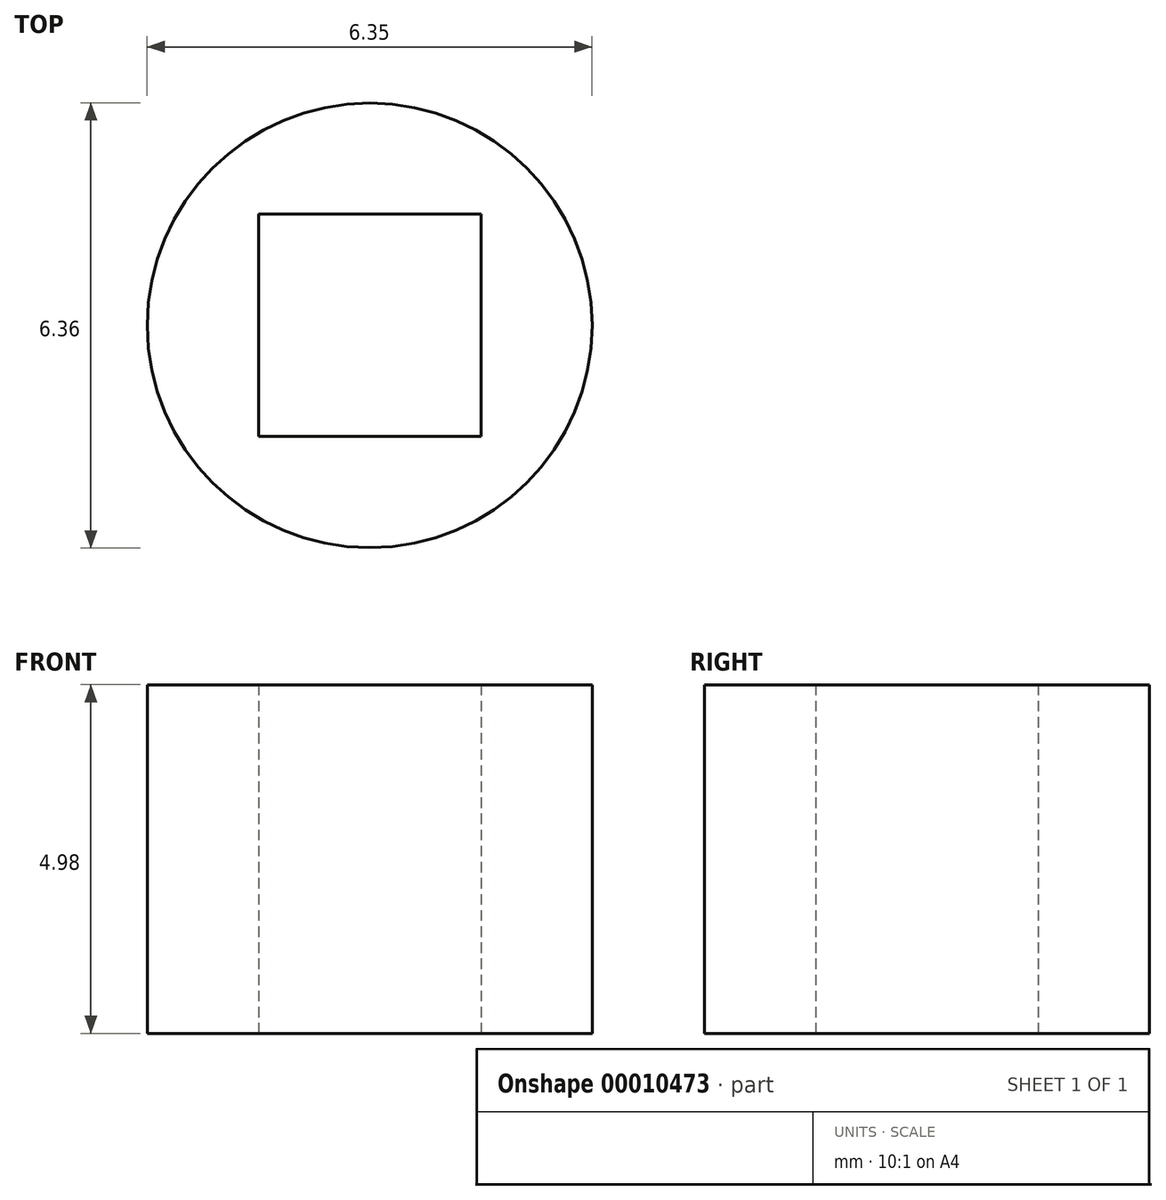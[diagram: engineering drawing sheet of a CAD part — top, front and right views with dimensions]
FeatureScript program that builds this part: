
annotation { "Feature Type Name" : "Feature", "Feature Type Description" : "" }
export const myFeature = defineFeature(function(context is Context, id is Id, definition is map)
    precondition{}
    {
        {
            var Q0;
            Q0=qCreatedBy(makeId("Top.planeOp"),FACE);
            var sketch = newSketch(context, id + "F0", { "sketchPlane" : qUnion([Q0])});
            skCircle(sketch, "E0", {"center": v(-1.07, 0) * mm, "radius": 3.18 * mm});
            skLineSegment(sketch, "E1.rect.bottom", {"start": v(-2.66, 1.59) * mm, "end": v(0.51, 1.59) * mm});
            skLineSegment(sketch, "E1.rect.top", {"start": v(-2.66, -1.59) * mm, "end": v(0.51, -1.59) * mm});
            skLineSegment(sketch, "E1.rect.left", {"start": v(-2.66, 1.59) * mm, "end": v(-2.66, -1.59) * mm});
            skLineSegment(sketch, "E1.rect.right", {"start": v(0.51, 1.59) * mm, "end": v(0.51, -1.59) * mm});
            skSolve(sketch);
        }
        {
            var Q0;
            Q0 = qSketchRegion(id + "F0", true);
            extrude(context, id + "F1", {"entities" : qUnion([Q0]), "depth" : 4.98 * mm});
        }
    });
